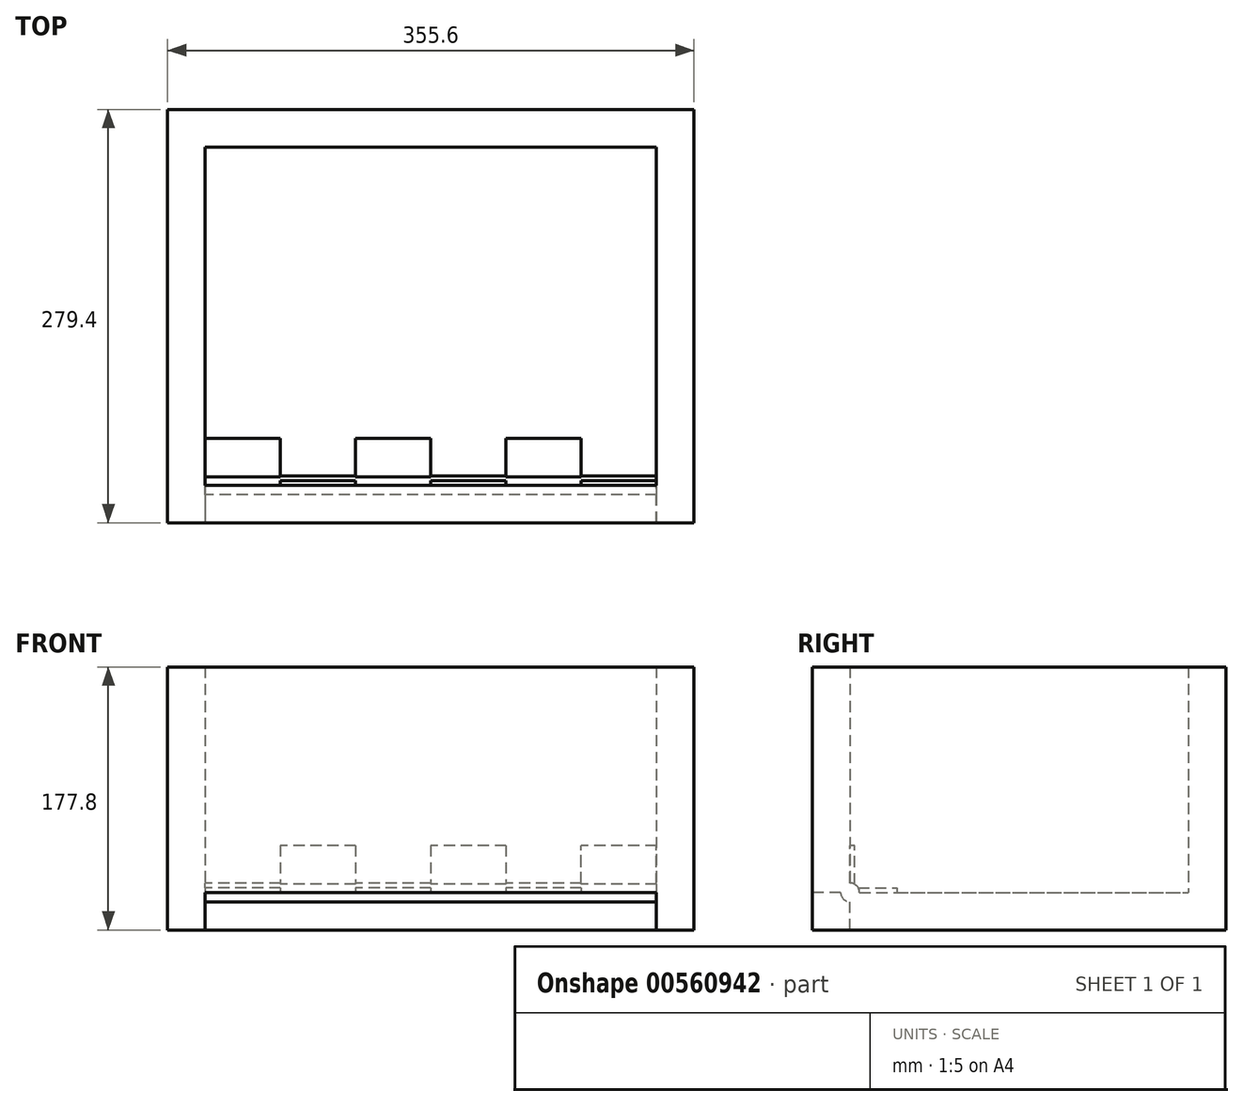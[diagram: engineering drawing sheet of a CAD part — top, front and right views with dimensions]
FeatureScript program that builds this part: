
annotation { "Feature Type Name" : "Feature", "Feature Type Description" : "" }
export const myFeature = defineFeature(function(context is Context, id is Id, definition is map)
    precondition{}
    {
        {
            var Q0;
            Q0=qCreatedBy(makeId("Top.planeOp"),FACE);
            var sketch = newSketch(context, id + "F0", { "sketchPlane" : qUnion([Q0])});
            skLineSegment(sketch, "E0.bottom", {"start": v(0, 0) * mm, "end": v(304.8, 0) * mm});
            skLineSegment(sketch, "E0.top", {"start": v(0, 228.6) * mm, "end": v(304.8, 228.6) * mm});
            skLineSegment(sketch, "E0.left", {"start": v(0, 0) * mm, "end": v(0, 228.6) * mm});
            skLineSegment(sketch, "E0.right", {"start": v(304.8, 0) * mm, "end": v(304.8, 228.6) * mm});
            skLineSegment(sketch, "E1.bottom", {"start": v(-25.4, -25.4) * mm, "end": v(330.2, -25.4) * mm});
            skLineSegment(sketch, "E1.top", {"start": v(-25.4, 254) * mm, "end": v(330.2, 254) * mm});
            skLineSegment(sketch, "E1.left", {"start": v(-25.4, -25.4) * mm, "end": v(-25.4, 254) * mm});
            skLineSegment(sketch, "E1.right", {"start": v(330.2, -25.4) * mm, "end": v(330.2, 254) * mm});
            skPoint(sketch, "E1.middle", {"position": v(152.4, 114.3) * mm});
            skPoint(sketch, "E1.middle.positionSnap0", {"position": v(0, 114.3) * mm});
            skPoint(sketch, "E1.middle.positionSnap1", {"position": v(152.4, 228.6) * mm});
            skPoint(sketch, "E1.centerSnap0", {"position": v(0, 114.3) * mm});
            skPoint(sketch, "E1.centerSnap1", {"position": v(152.4, 228.6) * mm});
            skLineSegment(sketch, "E2", {"start": v(304.8, 0) * mm, "end": v(304.8, -25.4) * mm});
            skLineSegment(sketch, "E3", {"start": v(0, 0) * mm, "end": v(0, -25.4) * mm});
            skSolve(sketch);
        }
        {
            var Q0;
            Q0=makeQuery(id+"F0.imprint","IMPRINT",FACE,{"disambiguationData":[TD([[makeQuery(id+"F0.imprint","IMPRINT",EDGE,{"derivedFrom":sQuery(id+"F0.wireOp",EDGE,"E0.bottom")}),1.0]])]});
            extrude(context, id + "F1", {"entities" : qUnion([Q0]), "oppositeDirection" : true, "depth" : 25.4 * mm, "offsetDistance" : 25.4 * mm});
        }
        {
            var Q0;
            Q0=makeQuery(id+"F0.imprint","IMPRINT",FACE,{"disambiguationData":[TD([[makeQuery(id+"F0.imprint","IMPRINT",EDGE,{"derivedFrom":sQuery(id+"F0.wireOp",EDGE,"E0.top")}),1.0]])]});
            extrude(context, id + "F2", {"entities" : qUnion([Q0]), "operationType" : NewBodyOperationType.ADD, "depth" : 152.4 * mm, "offsetDistance" : 25.4 * mm, "hasSecondDirection" : true, "secondDirectionOppositeDirection" : true, "secondDirectionDepth" : 25.4 * mm});
        }
        {
            var Q0;
            Q0=makeQuery(id+"F0.imprint","IMPRINT",FACE,{"disambiguationData":[TD([[makeQuery(id+"F0.imprint","IMPRINT",EDGE,{"derivedFrom":sQuery(id+"F0.wireOp",EDGE,"E0.bottom")}),-1.0]])]});
            extrude(context, id + "F3", {"entities" : qUnion([Q0]), "depth" : 152.4 * mm, "offsetDistance" : 25.4 * mm});
        }
        {
            var Q0;
            Q0=qCreatedBy(makeId("Right.planeOp"),FACE);
            var sketch = newSketch(context, id + "F4", { "sketchPlane" : qUnion([Q0])});
            skCircle(sketch, "E4", {"center": v(0, 0) * mm, "radius": 6.35 * mm});
            skCircle(sketch, "E5", {"center": v(0, 0) * mm, "radius": 3.18 * mm});
            skSolve(sketch);
        }
        {
            var Q0;
            Q0=makeQuery(id+"F4.imprint","IMPRINT",FACE,{"disambiguationData":[TD([[makeQuery(id+"F4.imprint","IMPRINT",EDGE,{"derivedFrom":sQuery(id+"F4.wireOp",EDGE,"E5")}),1.0]])]});
            var Q1;
            Q1=makeQuery(id+"F4.imprint","IMPRINT",FACE,{"disambiguationData":[TD([[makeQuery(id+"F4.imprint","IMPRINT",EDGE,{"derivedFrom":sQuery(id+"F4.wireOp",EDGE,"E4")}),1.0]])]});
            var Q2;
            Q2=makeQuery(id+"F2.opExtrude","SWEPT_FACE",FACE,{"disambiguationData":[OSD([sQuery(id+"F0.wireOp",EDGE,"E0.right"),sQuery(id+"F0.wireOp",EDGE,"E2")])]});
            extrude(context, id + "F5", {"entities" : qUnion([Q0, Q1]), "operationType" : NewBodyOperationType.REMOVE, "endBound" : BoundingType.UP_TO_SURFACE, "depth" : 25.4 * mm, "endBoundEntityFace" : qUnion([Q2]), "offsetDistance" : 25.4 * mm});
        }
        {
            var Q0;
            Q0=makeQuery(id+"F4.imprint","IMPRINT",FACE,{"disambiguationData":[TD([[makeQuery(id+"F4.imprint","IMPRINT",EDGE,{"derivedFrom":sQuery(id+"F4.wireOp",EDGE,"E5")}),1.0]])]});
            var Q1;
            {var subQ0=sQuery(id+"F0.wireOp",EDGE,"E2");var subQ1=sQuery(id+"F0.wireOp",EDGE,"E0.right");Q1=makeQuery(id+"F5.boolean.opBoolean","MERGE",FACE,{"derivedFrom":[makeQuery(id+"F2.opExtrude","SWEPT_FACE",FACE,{"disambiguationData":[OSD([subQ1,subQ0])]}),makeQuery(id+"F5.opExtrude","CAP_FACE",FACE,{"disambiguationData":[OSD([subQ1,subQ0])],"isStart":false})]});}
            extrude(context, id + "F6", {"entities" : qUnion([Q0]), "operationType" : NewBodyOperationType.ADD, "endBound" : BoundingType.UP_TO_SURFACE, "depth" : 25.4 * mm, "endBoundEntityFace" : qUnion([Q1]), "offsetDistance" : 25.4 * mm});
        }
        {
            var Q0;
            Q0=makeQuery(id+"F4.imprint","IMPRINT",FACE,{"disambiguationData":[TD([[makeQuery(id+"F4.imprint","IMPRINT",EDGE,{"derivedFrom":sQuery(id+"F4.wireOp",EDGE,"E4")}),1.0]])]});
            var Q1;
            {var subQ0=sQuery(id+"F0.wireOp",EDGE,"E2");var subQ1=sQuery(id+"F0.wireOp",EDGE,"E0.right");Q1=makeQuery(id+"F5.boolean.opBoolean","MERGE",FACE,{"derivedFrom":[makeQuery(id+"F2.opExtrude","SWEPT_FACE",FACE,{"disambiguationData":[OSD([subQ1,subQ0])]}),makeQuery(id+"F5.opExtrude","CAP_FACE",FACE,{"disambiguationData":[OSD([subQ1,subQ0])],"isStart":false})]});}
            extrude(context, id + "F7", {"entities" : qUnion([Q0]), "endBound" : BoundingType.UP_TO_SURFACE, "depth" : 25.4 * mm, "endBoundEntityFace" : qUnion([Q1]), "offsetDistance" : 25.4 * mm});
        }
        {
            var Q0;
            Q0=makeQuery(id+"F3.opExtrude","SWEPT_FACE",FACE,{"disambiguationData":[OSD([sQuery(id+"F0.wireOp",EDGE,"E0.bottom")])]});
            var sketch = newSketch(context, id + "F8", { "sketchPlane" : qUnion([Q0])});
            skLineSegment(sketch, "E6.bottom", {"start": v(-304.8, 0) * mm, "end": v(-254, 0) * mm});
            skLineSegment(sketch, "E6.top", {"start": v(-304.8, 31.75) * mm, "end": v(-254, 31.75) * mm});
            skLineSegment(sketch, "E6.left", {"start": v(-304.8, 0) * mm, "end": v(-304.8, 31.75) * mm});
            skLineSegment(sketch, "E6.right", {"start": v(-254, 0) * mm, "end": v(-254, 31.75) * mm});
            skPoint(sketch, "E7.oppositeSnap0", {"position": v(-152.4, 0) * mm});
            skLineSegment(sketch, "E7.bottom", {"start": v(-203.2, 31.75) * mm, "end": v(-152.4, 31.75) * mm});
            skLineSegment(sketch, "E7.top", {"start": v(-203.2, 0) * mm, "end": v(-152.4, 0) * mm});
            skLineSegment(sketch, "E7.left", {"start": v(-203.2, 31.75) * mm, "end": v(-203.2, 0) * mm});
            skLineSegment(sketch, "E7.right", {"start": v(-152.4, 31.75) * mm, "end": v(-152.4, 0) * mm});
            skLineSegment(sketch, "E8.bottom", {"start": v(-101.6, 31.75) * mm, "end": v(-50.8, 31.75) * mm});
            skLineSegment(sketch, "E8.top", {"start": v(-101.6, 0) * mm, "end": v(-50.8, 0) * mm});
            skLineSegment(sketch, "E8.left", {"start": v(-101.6, 31.75) * mm, "end": v(-101.6, 0) * mm});
            skLineSegment(sketch, "E8.right", {"start": v(-50.8, 31.75) * mm, "end": v(-50.8, 0) * mm});
            skLineSegment(sketch, "E9", {"start": v(-50.8, 31.75) * mm, "end": v(0, 31.75) * mm, "construction": true});
            skLineSegment(sketch, "E10", {"start": v(-101.6, 31.75) * mm, "end": v(-152.4, 31.75) * mm, "construction": true});
            skLineSegment(sketch, "E11", {"start": v(-203.2, 31.75) * mm, "end": v(-254, 31.75) * mm, "construction": true});
            skSolve(sketch);
        }
        {
            var Q0;
            Q0=makeQuery(id+"F0.imprint","IMPRINT",FACE,{"disambiguationData":[TD([[makeQuery(id+"F0.imprint","IMPRINT",EDGE,{"derivedFrom":sQuery(id+"F0.wireOp",EDGE,"E0.bottom")}),1.0]])]});
            var sketch = newSketch(context, id + "F9", { "sketchPlane" : qUnion([Q0])});
            skLineSegment(sketch, "E12.bottom", {"start": v(0, 0) * mm, "end": v(50.8, 0) * mm});
            skLineSegment(sketch, "E12.top", {"start": v(0, 31.75) * mm, "end": v(50.8, 31.75) * mm});
            skLineSegment(sketch, "E12.left", {"start": v(0, 0) * mm, "end": v(0, 31.75) * mm});
            skLineSegment(sketch, "E12.right", {"start": v(50.8, 0) * mm, "end": v(50.8, 31.75) * mm});
            skLineSegment(sketch, "E13.bottom", {"start": v(101.6, 0) * mm, "end": v(152.4, 0) * mm});
            skLineSegment(sketch, "E13.top", {"start": v(101.6, 31.75) * mm, "end": v(152.4, 31.75) * mm});
            skLineSegment(sketch, "E13.left", {"start": v(101.6, 0) * mm, "end": v(101.6, 31.75) * mm});
            skLineSegment(sketch, "E13.right", {"start": v(152.4, 0) * mm, "end": v(152.4, 31.75) * mm});
            skLineSegment(sketch, "E14.bottom", {"start": v(203.2, 0) * mm, "end": v(254, 0) * mm});
            skLineSegment(sketch, "E14.top", {"start": v(203.2, 31.75) * mm, "end": v(254, 31.75) * mm});
            skLineSegment(sketch, "E14.left", {"start": v(203.2, 0) * mm, "end": v(203.2, 31.75) * mm});
            skLineSegment(sketch, "E14.right", {"start": v(254, 0) * mm, "end": v(254, 31.75) * mm});
            skSolve(sketch);
        }
        {
            var Q0;
            Q0 = qSketchRegion(id + "F8", true);
            extrude(context, id + "F10", {"entities" : qUnion([Q0]), "operationType" : NewBodyOperationType.ADD, "depth" : 3.17 * mm, "offsetDistance" : 25.4 * mm});
        }
        {
            var Q0;
            Q0 = qSketchRegion(id + "F9", true);
            extrude(context, id + "F11", {"entities" : qUnion([Q0]), "operationType" : NewBodyOperationType.ADD, "depth" : 3.17 * mm, "offsetDistance" : 25.4 * mm});
        }
    });
